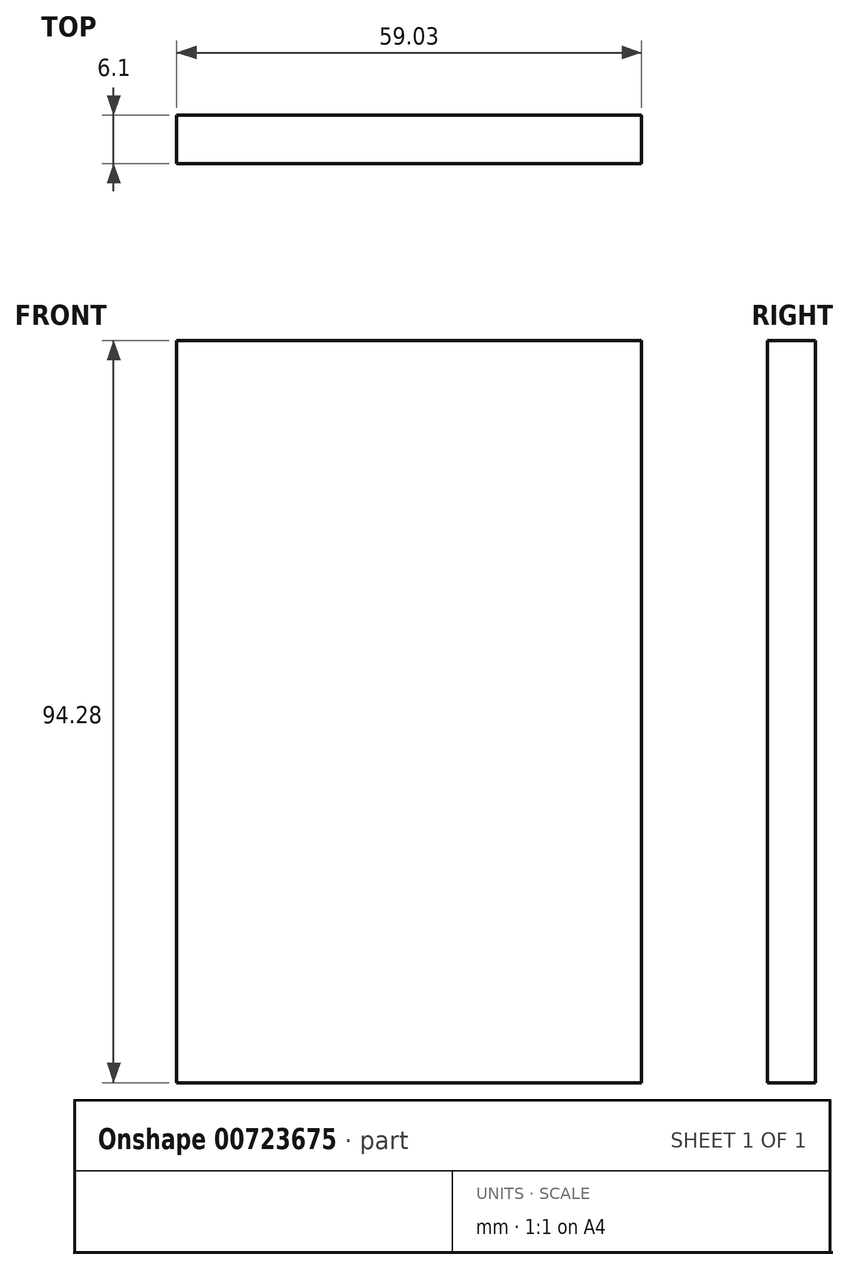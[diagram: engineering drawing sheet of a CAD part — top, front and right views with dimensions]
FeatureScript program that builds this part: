
annotation { "Feature Type Name" : "Feature", "Feature Type Description" : "" }
export const myFeature = defineFeature(function(context is Context, id is Id, definition is map)
    precondition{}
    {
        {
            var Q0;
            Q0=qCreatedBy(makeId("Front.planeOp"),FACE);
            var sketch = newSketch(context, id + "F0", { "sketchPlane" : qUnion([Q0])});
            skLineSegment(sketch, "E0.bottom", {"start": v(-31.36, 35.22) * mm, "end": v(27.67, 35.22) * mm});
            skLineSegment(sketch, "E0.top", {"start": v(-31.36, -59.06) * mm, "end": v(27.67, -59.06) * mm});
            skLineSegment(sketch, "E0.left", {"start": v(-31.36, 35.22) * mm, "end": v(-31.36, -59.06) * mm});
            skLineSegment(sketch, "E0.right", {"start": v(27.67, 35.22) * mm, "end": v(27.67, -59.06) * mm});
            skSolve(sketch);
        }
        {
            var Q0;
            Q0=makeQuery(id+"F0.imprint","IMPRINT",FACE,{"disambiguationData":[TD([[makeQuery(id+"F0.imprint","IMPRINT",EDGE,{"derivedFrom":sQuery(id+"F0.wireOp",EDGE,"E0.bottom")}),-1.0]])]});
            extrude(context, id + "F1", {"entities" : qUnion([Q0]), "depth" : 6.1 * mm, "offsetDistance" : 25 * mm});
        }
    });
